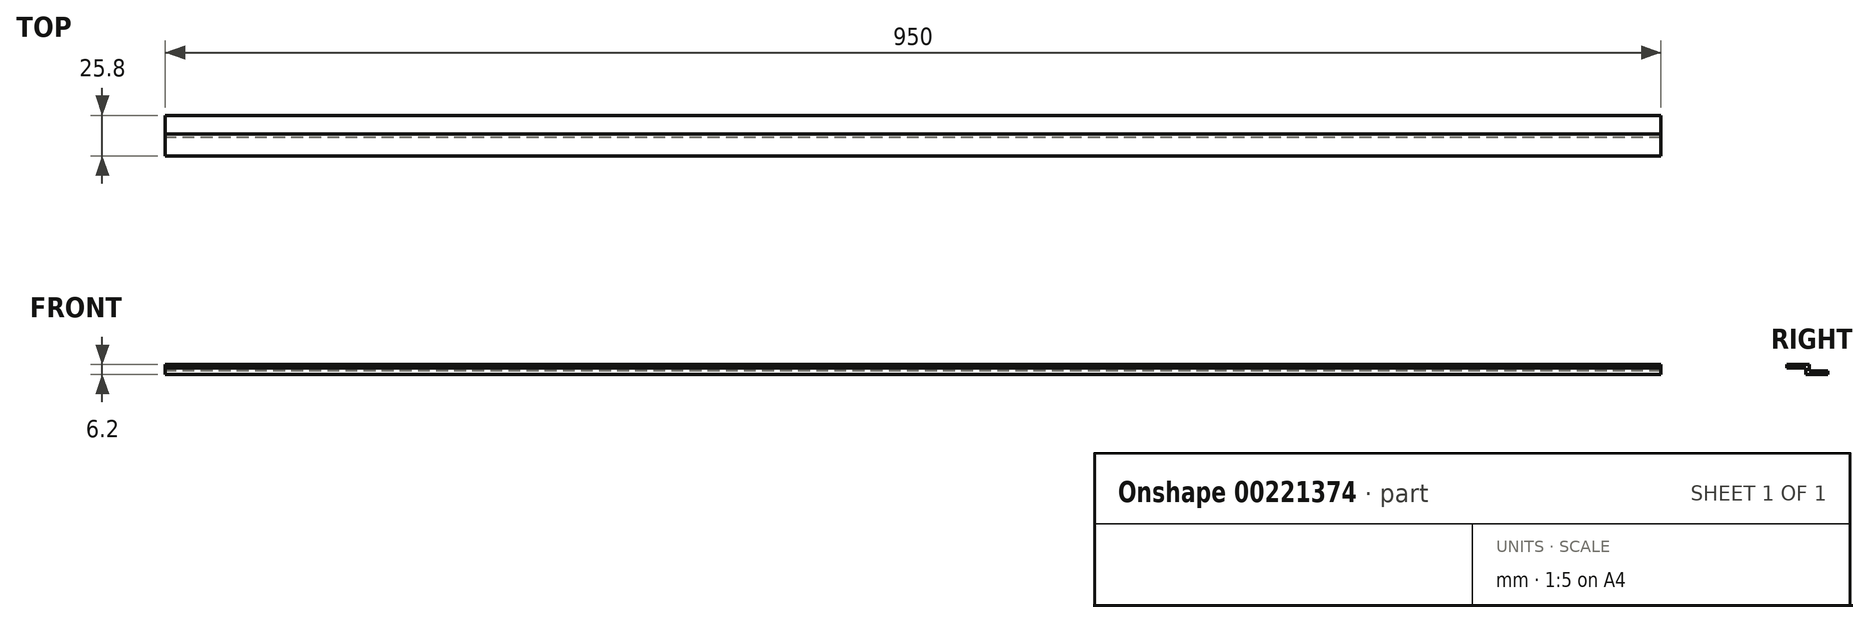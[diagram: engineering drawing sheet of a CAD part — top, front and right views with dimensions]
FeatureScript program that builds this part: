
annotation { "Feature Type Name" : "Feature", "Feature Type Description" : "" }
export const myFeature = defineFeature(function(context is Context, id is Id, definition is map)
    precondition{}
    {
        {
            var Q0;
            Q0=qCreatedBy(makeId("Right.planeOp"),FACE);
            var sketch = newSketch(context, id + "F0", { "sketchPlane" : qUnion([Q0])});
            skLineSegment(sketch, "E0", {"start": v(0, 0) * mm, "end": v(0, -4) * mm});
            skLineSegment(sketch, "E1", {"start": v(0, -4) * mm, "end": v(11.8, -4) * mm});
            skLineSegment(sketch, "E2", {"start": v(11.8, -4) * mm, "end": v(11.8, -6.2) * mm});
            skLineSegment(sketch, "E3", {"start": v(11.8, -6.2) * mm, "end": v(-2.2, -6.2) * mm});
            skLineSegment(sketch, "E4", {"start": v(-2.2, -6.2) * mm, "end": v(-2.2, -2.2) * mm});
            skLineSegment(sketch, "E5", {"start": v(-2.2, -2.2) * mm, "end": v(-14, -2.2) * mm});
            skLineSegment(sketch, "E6", {"start": v(-14, -2.2) * mm, "end": v(-14, 0) * mm});
            skLineSegment(sketch, "E7", {"start": v(-14, 0) * mm, "end": v(0, 0) * mm});
            skSolve(sketch);
        }
        {
            var Q0;
            Q0=qSketchRegion(id+"F0",true);
            extrude(context, id + "F1", {"entities" : qUnion([Q0]), "depth" : 950 * mm, "symmetric" : true});
        }
    });
